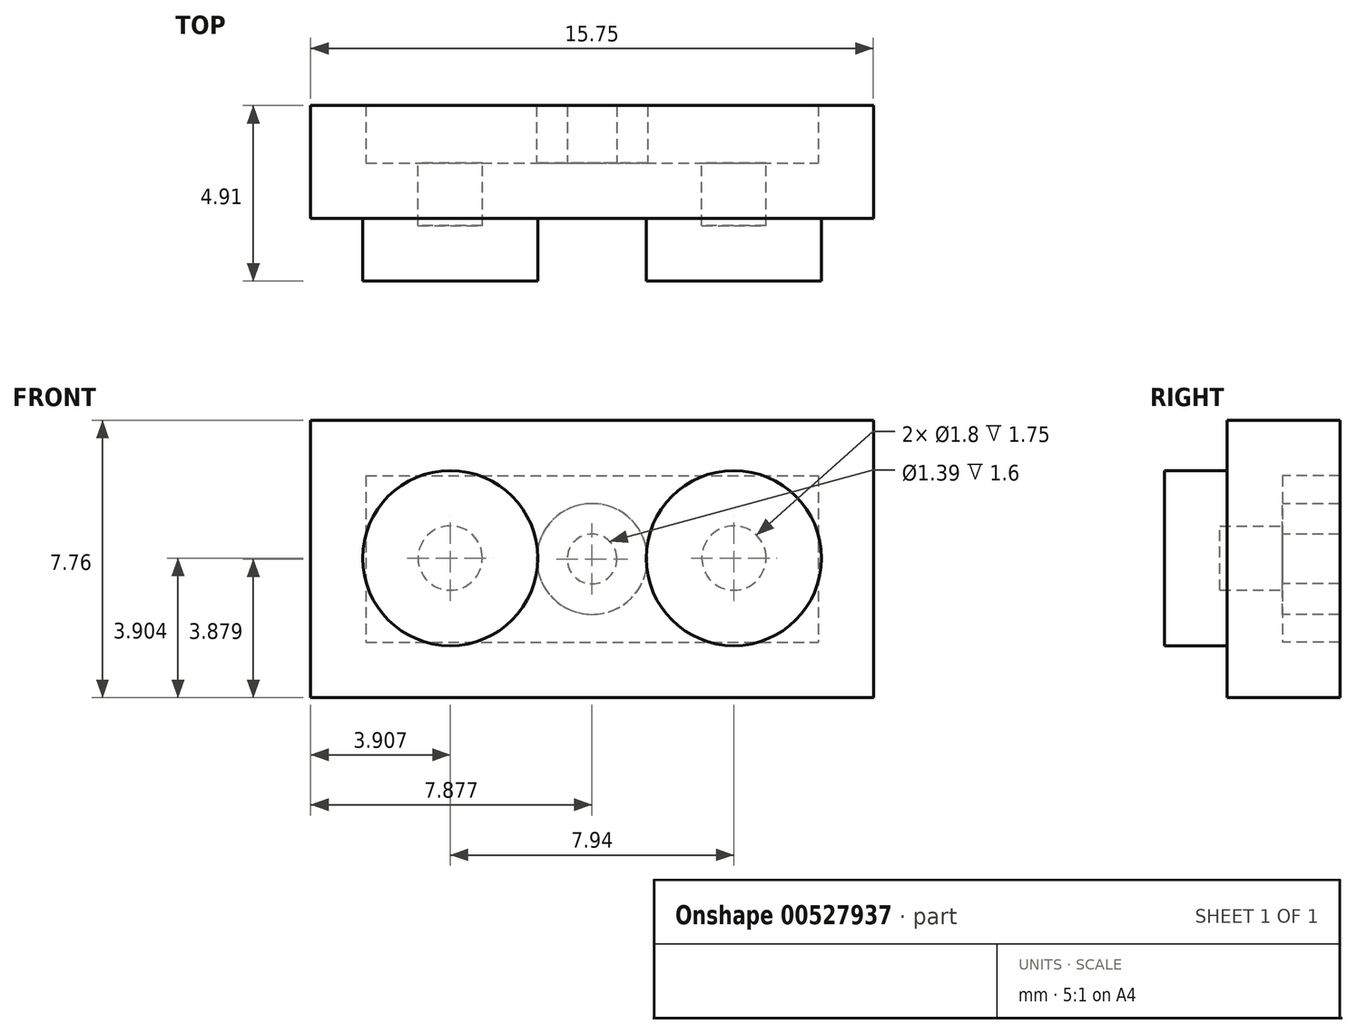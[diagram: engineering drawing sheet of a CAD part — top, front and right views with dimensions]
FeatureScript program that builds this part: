
annotation { "Feature Type Name" : "Feature", "Feature Type Description" : "" }
export const myFeature = defineFeature(function(context is Context, id is Id, definition is map)
    precondition{}
    {
        {
            var Q0;
            Q0=qCreatedBy(makeId("Front.planeOp"),FACE);
            var sketch = newSketch(context, id + "F0", { "sketchPlane" : qUnion([Q0])});
            skLineSegment(sketch, "E0.bottom", {"start": v(0.6, 7.46) * mm, "end": v(16.34, 7.46) * mm});
            skLineSegment(sketch, "E0.top", {"start": v(0.6, -0.3) * mm, "end": v(16.34, -0.3) * mm});
            skLineSegment(sketch, "E0.left", {"start": v(0.6, 7.46) * mm, "end": v(0.6, -0.3) * mm});
            skLineSegment(sketch, "E0.right", {"start": v(16.34, 7.46) * mm, "end": v(16.34, -0.3) * mm});
            skSolve(sketch);
        }
        {
            var Q0;
            Q0=makeQuery(id+"F0.imprint","IMPRINT",FACE,{"disambiguationData":[TD([[makeQuery(id+"F0.imprint","IMPRINT",EDGE,{"derivedFrom":sQuery(id+"F0.wireOp",EDGE,"E0.bottom")}),-1.0]])]});
            extrude(context, id + "F1", {"entities" : qUnion([Q0]), "oppositeDirection" : true, "depth" : 3.16 * mm, "offsetDistance" : 25 * mm});
        }
        {
            var Q0;
            Q0=makeQuery(id+"F1.opExtrude","CAP_FACE",FACE,{"disambiguationData":[OSD([sQuery(id+"F0.wireOp",EDGE,"E0.bottom"),sQuery(id+"F0.wireOp",EDGE,"E0.top"),sQuery(id+"F0.wireOp",EDGE,"E0.left"),sQuery(id+"F0.wireOp",EDGE,"E0.right")])],"isStart":true});
            var sketch = newSketch(context, id + "F2", { "sketchPlane" : qUnion([Q0])});
            skCircle(sketch, "E1", {"center": v(4.5, 3.6) * mm, "radius": 2.45 * mm});
            skCircle(sketch, "E2", {"center": v(12.44, 3.6) * mm, "radius": 2.45 * mm});
            skSolve(sketch);
        }
        {
            var Q0;
            Q0=makeQuery(id+"F2.imprint","IMPRINT",FACE,{"disambiguationData":[TD([[makeQuery(id+"F2.imprint","IMPRINT",EDGE,{"derivedFrom":sQuery(id+"F2.wireOp",EDGE,"E1")}),1.0]])]});
            var Q1;
            Q1=makeQuery(id+"F2.imprint","IMPRINT",FACE,{"disambiguationData":[TD([[makeQuery(id+"F2.imprint","IMPRINT",EDGE,{"derivedFrom":sQuery(id+"F2.wireOp",EDGE,"E2")}),1.0]])]});
            extrude(context, id + "F3", {"entities" : qUnion([Q0, Q1]), "operationType" : NewBodyOperationType.ADD, "depth" : 1.75 * mm, "offsetDistance" : 25 * mm});
        }
        {
            var Q0;
            Q0=makeQuery(id+"F1.opExtrude","CAP_FACE",FACE,{"disambiguationData":[OSD([sQuery(id+"F0.wireOp",EDGE,"E0.bottom"),sQuery(id+"F0.wireOp",EDGE,"E0.top"),sQuery(id+"F0.wireOp",EDGE,"E0.left"),sQuery(id+"F0.wireOp",EDGE,"E0.right")])],"isStart":false});
            shell(context, id + "F4", {"entities" : qUnion([Q0]), "thickness" : 1.55 * mm});
        }
        {
            var Q0;
            Q0=makeQuery(id+"F4.opShell","OFFSET_FACE",FACE,{"disambiguationData":[OSD([sQuery(id+"F0.wireOp",EDGE,"E0.bottom"),sQuery(id+"F0.wireOp",EDGE,"E0.top"),sQuery(id+"F0.wireOp",EDGE,"E0.left"),sQuery(id+"F0.wireOp",EDGE,"E0.right")])]});
            var sketch = newSketch(context, id + "F5", { "sketchPlane" : qUnion([Q0])});
            skCircle(sketch, "E3", {"center": v(-8.47, 3.58) * mm, "radius": 1.55 * mm});
            skPoint(sketch, "E3.centerSnap0", {"position": v(-2.14, 3.58) * mm});
            skPoint(sketch, "E3.centerSnap1", {"position": v(-8.47, 5.9) * mm});
            skCircle(sketch, "E4", {"center": v(-8.47, 3.58) * mm, "radius": 0.7 * mm});
            skSolve(sketch);
        }
        {
            var Q0;
            Q0 = qSketchRegion(id + "F5", true);
            extrude(context, id + "F6", {"entities" : qUnion([Q0]), "operationType" : NewBodyOperationType.ADD, "depth" : 1.6 * mm, "offsetDistance" : 25 * mm});
        }
    });
